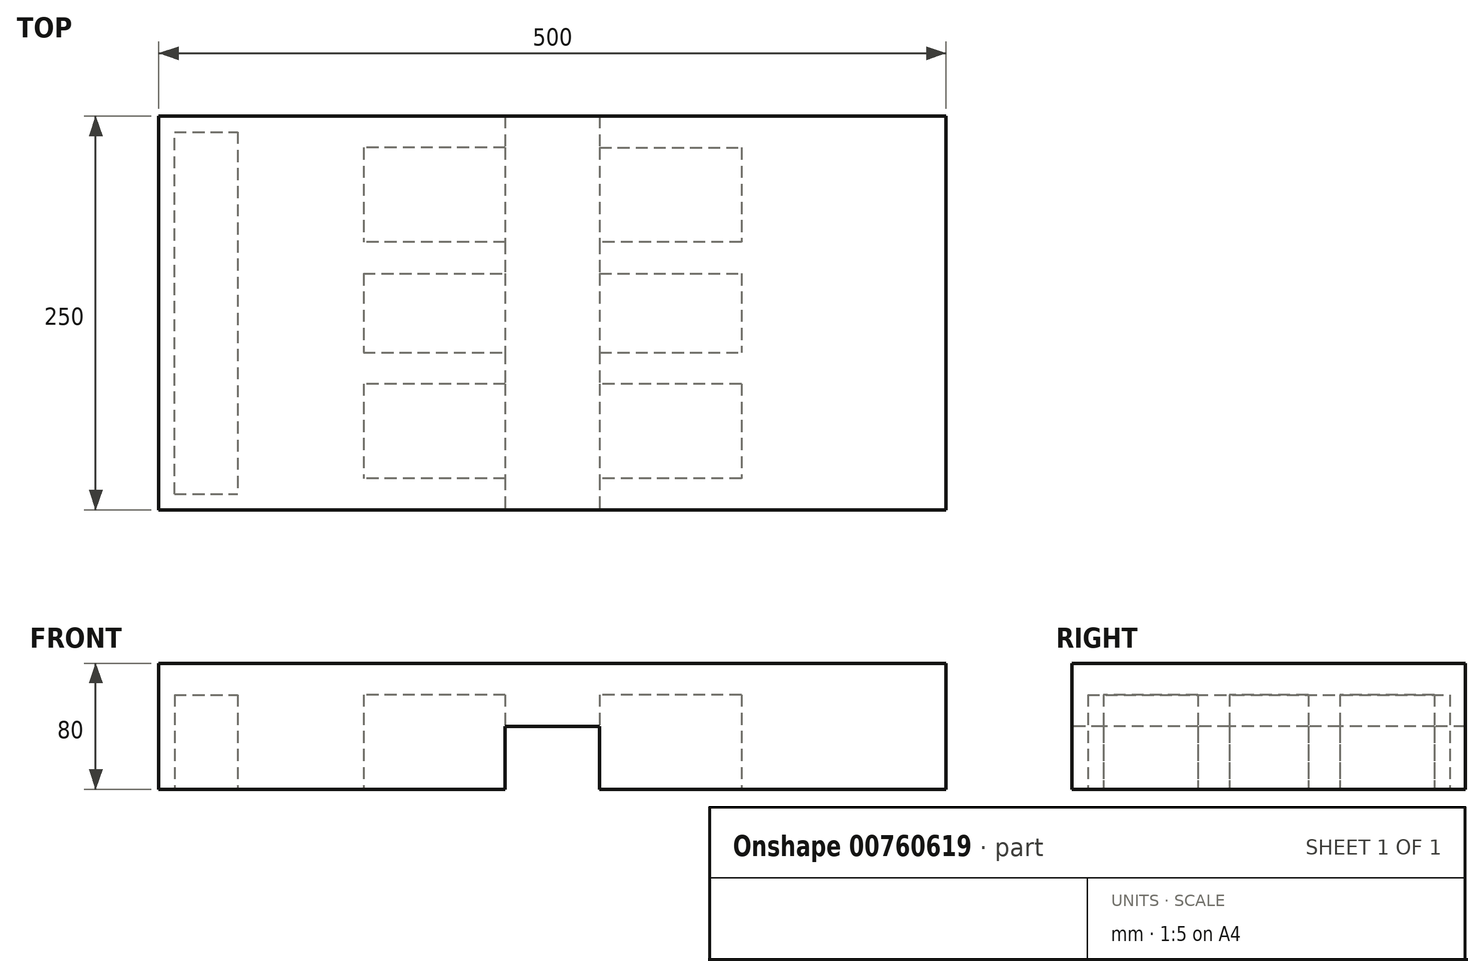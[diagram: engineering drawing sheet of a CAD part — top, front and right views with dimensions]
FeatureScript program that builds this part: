
annotation { "Feature Type Name" : "Feature", "Feature Type Description" : "" }
export const myFeature = defineFeature(function(context is Context, id is Id, definition is map)
    precondition{}
    {
        {
            var Q0;
            Q0=qCreatedBy(makeId("Top.planeOp"),FACE);
            var sketch = newSketch(context, id + "F0", { "sketchPlane" : qUnion([Q0])});
            skLineSegment(sketch, "E0.bottom", {"start": v(-250, 125) * mm, "end": v(250, 125) * mm});
            skLineSegment(sketch, "E0.top", {"start": v(-250, -125) * mm, "end": v(250, -125) * mm});
            skLineSegment(sketch, "E0.left", {"start": v(-250, 125) * mm, "end": v(-250, -125) * mm});
            skLineSegment(sketch, "E0.right", {"start": v(250, 125) * mm, "end": v(250, -125) * mm});
            skPoint(sketch, "E0.middle", {"position": v(0, 0) * mm});
            skLineSegment(sketch, "E1", {"start": v(-250, 0) * mm, "end": v(250, 0) * mm});
            skLineSegment(sketch, "E2", {"start": v(0, 125) * mm, "end": v(0, -125) * mm});
            skLineSegment(sketch, "E3", {"start": v(-30, 125) * mm, "end": v(-30, -125) * mm});
            skLineSegment(sketch, "E4", {"start": v(30, 125) * mm, "end": v(30, -125) * mm});
            skLineSegment(sketch, "E5", {"start": v(120, 125) * mm, "end": v(120, -125) * mm});
            skLineSegment(sketch, "E6", {"start": v(-120, 125) * mm, "end": v(-120, -125) * mm});
            skLineSegment(sketch, "E7", {"start": v(30, 105) * mm, "end": v(120, 105) * mm});
            skLineSegment(sketch, "E8", {"start": v(120, 45) * mm, "end": v(30, 45) * mm});
            skLineSegment(sketch, "E9", {"start": v(120, -45) * mm, "end": v(30, -45) * mm});
            skLineSegment(sketch, "E10", {"start": v(120, -105) * mm, "end": v(30, -105) * mm});
            skLineSegment(sketch, "E11", {"start": v(-30, -105) * mm, "end": v(-120, -105) * mm});
            skLineSegment(sketch, "E12", {"start": v(-30, -45) * mm, "end": v(-120, -45) * mm});
            skLineSegment(sketch, "E13", {"start": v(-30, 45) * mm, "end": v(-120, 45) * mm});
            skLineSegment(sketch, "E14", {"start": v(-30, 105) * mm, "end": v(-120, 105) * mm});
            skLineSegment(sketch, "E15", {"start": v(-120, 25) * mm, "end": v(120, 25) * mm});
            skLineSegment(sketch, "E16", {"start": v(-120, -25) * mm, "end": v(120, -25) * mm});
            skLineSegment(sketch, "E17", {"start": v(-250, 115) * mm, "end": v(-120, 115) * mm});
            skLineSegment(sketch, "E18", {"start": v(-250, -115) * mm, "end": v(-120, -115) * mm});
            skLineSegment(sketch, "E19", {"start": v(-240, -115) * mm, "end": v(-240, 115) * mm});
            skLineSegment(sketch, "E20", {"start": v(-200, 115) * mm, "end": v(-200, -115) * mm});
            skSolve(sketch);
        }
        {
            var Q0;
            {var subQ1=sQuery(id+"F0.wireOp",EDGE,"E0.bottom");var subQ5=sQuery(id+"F0.wireOp",EDGE,"E0.left");var subQ6=makeQuery(id+"F0.imprint","INTERSECT",VERTEX,{"derivedFrom":[subQ1,subQ5]});Q0=makeQuery(id+"F0.imprint","IMPRINT",FACE,{"disambiguationData":[TD([[makeQuery(id+"F0.imprint","IMPRINT",EDGE,{"disambiguationData":[TD([[subQ6,-1.0]])],"derivedFrom":subQ1}),-1.0]])]});}
            var Q1;
            {var subQ0=sQuery(id+"F0.wireOp",EDGE,"E1");var subQ1=sQuery(id+"F0.wireOp",EDGE,"E0.left");var subQ2=makeQuery(id+"F0.imprint","INTERSECT",VERTEX,{"derivedFrom":[subQ1,subQ0]});Q1=makeQuery(id+"F0.imprint","IMPRINT",FACE,{"disambiguationData":[TD([[makeQuery(id+"F0.imprint","IMPRINT",EDGE,{"disambiguationData":[TD([[subQ2,1.0]])],"derivedFrom":subQ1}),1.0]])]});}
            var Q2;
            {var subQ0=sQuery(id+"F0.wireOp",EDGE,"E1");var subQ1=sQuery(id+"F0.wireOp",EDGE,"E0.left");var subQ2=makeQuery(id+"F0.imprint","INTERSECT",VERTEX,{"derivedFrom":[subQ1,subQ0]});Q2=makeQuery(id+"F0.imprint","IMPRINT",FACE,{"disambiguationData":[TD([[makeQuery(id+"F0.imprint","IMPRINT",EDGE,{"disambiguationData":[TD([[subQ2,-1.0]])],"derivedFrom":subQ1}),1.0]])]});}
            var Q3;
            {var subQ1=sQuery(id+"F0.wireOp",EDGE,"E0.left");var subQ4=sQuery(id+"F0.wireOp",EDGE,"E0.top");var subQ5=makeQuery(id+"F0.imprint","INTERSECT",VERTEX,{"derivedFrom":[subQ4,subQ1]});Q3=makeQuery(id+"F0.imprint","IMPRINT",FACE,{"disambiguationData":[TD([[makeQuery(id+"F0.imprint","IMPRINT",EDGE,{"disambiguationData":[TD([[subQ5,-1.0]])],"derivedFrom":subQ4}),1.0]])]});}
            var Q4;
            {var subQ4=sQuery(id+"F0.wireOp",EDGE,"E14");Q4=makeQuery(id+"F0.imprint","IMPRINT",FACE,{"disambiguationData":[TD([[makeQuery(id+"F0.imprint","IMPRINT",EDGE,{"derivedFrom":subQ4}),-1.0]])]});}
            var Q5;
            {var subQ1=sQuery(id+"F0.wireOp",EDGE,"E0.bottom");var subQ5=sQuery(id+"F0.wireOp",EDGE,"E2");var subQ6=makeQuery(id+"F0.imprint","INTERSECT",VERTEX,{"derivedFrom":[subQ1,subQ5]});Q5=makeQuery(id+"F0.imprint","IMPRINT",FACE,{"disambiguationData":[TD([[makeQuery(id+"F0.imprint","IMPRINT",EDGE,{"disambiguationData":[TD([[subQ6,1.0]])],"derivedFrom":subQ1}),-1.0]])]});}
            var Q6;
            {var subQ5=sQuery(id+"F0.wireOp",EDGE,"E7");Q6=makeQuery(id+"F0.imprint","IMPRINT",FACE,{"disambiguationData":[TD([[makeQuery(id+"F0.imprint","IMPRINT",EDGE,{"derivedFrom":subQ5}),1.0]])]});}
            var Q7;
            {var subQ3=sQuery(id+"F0.wireOp",EDGE,"E2");var subQ4=sQuery(id+"F0.wireOp",EDGE,"E0.bottom");var subQ5=makeQuery(id+"F0.imprint","INTERSECT",VERTEX,{"derivedFrom":[subQ4,subQ3]});Q7=makeQuery(id+"F0.imprint","IMPRINT",FACE,{"disambiguationData":[TD([[makeQuery(id+"F0.imprint","IMPRINT",EDGE,{"disambiguationData":[TD([[subQ5,-1.0]])],"derivedFrom":subQ4}),-1.0]])]});}
            var Q8;
            {var subQ0=sQuery(id+"F0.wireOp",EDGE,"E13");Q8=makeQuery(id+"F0.imprint","IMPRINT",FACE,{"disambiguationData":[TD([[makeQuery(id+"F0.imprint","IMPRINT",EDGE,{"derivedFrom":subQ0}),1.0]])]});}
            var Q9;
            {var subQ0=sQuery(id+"F0.wireOp",EDGE,"E12");Q9=makeQuery(id+"F0.imprint","IMPRINT",FACE,{"disambiguationData":[TD([[makeQuery(id+"F0.imprint","IMPRINT",EDGE,{"derivedFrom":subQ0}),-1.0]])]});}
            var Q10;
            {var subQ4=sQuery(id+"F0.wireOp",EDGE,"E11");Q10=makeQuery(id+"F0.imprint","IMPRINT",FACE,{"disambiguationData":[TD([[makeQuery(id+"F0.imprint","IMPRINT",EDGE,{"derivedFrom":subQ4}),1.0]])]});}
            var Q11;
            {var subQ5=sQuery(id+"F0.wireOp",EDGE,"E2");var subQ6=sQuery(id+"F0.wireOp",EDGE,"E0.top");var subQ7=makeQuery(id+"F0.imprint","INTERSECT",VERTEX,{"derivedFrom":[subQ6,subQ5]});Q11=makeQuery(id+"F0.imprint","IMPRINT",FACE,{"disambiguationData":[TD([[makeQuery(id+"F0.imprint","IMPRINT",EDGE,{"disambiguationData":[TD([[subQ7,1.0]])],"derivedFrom":subQ6}),1.0]])]});}
            var Q12;
            {var subQ5=sQuery(id+"F0.wireOp",EDGE,"E2");var subQ6=sQuery(id+"F0.wireOp",EDGE,"E0.top");var subQ7=makeQuery(id+"F0.imprint","INTERSECT",VERTEX,{"derivedFrom":[subQ6,subQ5]});Q12=makeQuery(id+"F0.imprint","IMPRINT",FACE,{"disambiguationData":[TD([[makeQuery(id+"F0.imprint","IMPRINT",EDGE,{"disambiguationData":[TD([[subQ7,-1.0]])],"derivedFrom":subQ6}),1.0]])]});}
            var Q13;
            {var subQ0=sQuery(id+"F0.wireOp",EDGE,"E9");Q13=makeQuery(id+"F0.imprint","IMPRINT",FACE,{"disambiguationData":[TD([[makeQuery(id+"F0.imprint","IMPRINT",EDGE,{"derivedFrom":subQ0}),-1.0]])]});}
            var Q14;
            {var subQ0=sQuery(id+"F0.wireOp",EDGE,"E8");Q14=makeQuery(id+"F0.imprint","IMPRINT",FACE,{"disambiguationData":[TD([[makeQuery(id+"F0.imprint","IMPRINT",EDGE,{"derivedFrom":subQ0}),1.0]])]});}
            var Q15;
            {var subQ5=sQuery(id+"F0.wireOp",EDGE,"E10");Q15=makeQuery(id+"F0.imprint","IMPRINT",FACE,{"disambiguationData":[TD([[makeQuery(id+"F0.imprint","IMPRINT",EDGE,{"derivedFrom":subQ5}),1.0]])]});}
            var Q16;
            {var subQ1=sQuery(id+"F0.wireOp",EDGE,"E0.bottom");var subQ4=sQuery(id+"F0.wireOp",EDGE,"E0.right");var subQ5=makeQuery(id+"F0.imprint","INTERSECT",VERTEX,{"derivedFrom":[subQ1,subQ4]});Q16=makeQuery(id+"F0.imprint","IMPRINT",FACE,{"disambiguationData":[TD([[makeQuery(id+"F0.imprint","IMPRINT",EDGE,{"disambiguationData":[TD([[subQ5,1.0]])],"derivedFrom":subQ1}),-1.0]])]});}
            var Q17;
            {var subQ4=sQuery(id+"F0.wireOp",EDGE,"E0.right");var subQ5=sQuery(id+"F0.wireOp",EDGE,"E0.top");var subQ6=makeQuery(id+"F0.imprint","INTERSECT",VERTEX,{"derivedFrom":[subQ5,subQ4]});Q17=makeQuery(id+"F0.imprint","IMPRINT",FACE,{"disambiguationData":[TD([[makeQuery(id+"F0.imprint","IMPRINT",EDGE,{"disambiguationData":[TD([[subQ6,1.0]])],"derivedFrom":subQ5}),1.0]])]});}
            var Q18;
            {var subQ6=sQuery(id+"F0.wireOp",EDGE,"E20");var subQ8=sQuery(id+"F0.wireOp",EDGE,"E1");var subQ9=makeQuery(id+"F0.imprint","INTERSECT",VERTEX,{"derivedFrom":[subQ8,subQ6]});Q18=makeQuery(id+"F0.imprint","IMPRINT",FACE,{"disambiguationData":[TD([[makeQuery(id+"F0.imprint","IMPRINT",EDGE,{"disambiguationData":[TD([[subQ9,-1.0]])],"derivedFrom":subQ8}),1.0]])]});}
            var Q19;
            {var subQ4=sQuery(id+"F0.wireOp",EDGE,"E1");var subQ6=sQuery(id+"F0.wireOp",EDGE,"E20");var subQ7=makeQuery(id+"F0.imprint","INTERSECT",VERTEX,{"derivedFrom":[subQ4,subQ6]});Q19=makeQuery(id+"F0.imprint","IMPRINT",FACE,{"disambiguationData":[TD([[makeQuery(id+"F0.imprint","IMPRINT",EDGE,{"disambiguationData":[TD([[subQ7,-1.0]])],"derivedFrom":subQ4}),-1.0]])]});}
            var Q20;
            {var subQ0=sQuery(id+"F0.wireOp",EDGE,"E19");var subQ1=sQuery(id+"F0.wireOp",EDGE,"E1");var subQ2=makeQuery(id+"F0.imprint","INTERSECT",VERTEX,{"derivedFrom":[subQ1,subQ0]});Q20=makeQuery(id+"F0.imprint","IMPRINT",FACE,{"disambiguationData":[TD([[makeQuery(id+"F0.imprint","IMPRINT",EDGE,{"disambiguationData":[TD([[subQ2,-1.0]])],"derivedFrom":subQ1}),1.0]])]});}
            var Q21;
            {var subQ0=sQuery(id+"F0.wireOp",EDGE,"E19");var subQ1=sQuery(id+"F0.wireOp",EDGE,"E1");var subQ2=makeQuery(id+"F0.imprint","INTERSECT",VERTEX,{"derivedFrom":[subQ1,subQ0]});Q21=makeQuery(id+"F0.imprint","IMPRINT",FACE,{"disambiguationData":[TD([[makeQuery(id+"F0.imprint","IMPRINT",EDGE,{"disambiguationData":[TD([[subQ2,-1.0]])],"derivedFrom":subQ1}),-1.0]])]});}
            var Q22;
            {var subQ0=sQuery(id+"F0.wireOp",EDGE,"E13");Q22=makeQuery(id+"F0.imprint","IMPRINT",FACE,{"disambiguationData":[TD([[makeQuery(id+"F0.imprint","IMPRINT",EDGE,{"derivedFrom":subQ0}),-1.0]])]});}
            var Q23;
            {var subQ0=sQuery(id+"F0.wireOp",EDGE,"E6");var subQ1=sQuery(id+"F0.wireOp",EDGE,"E1");var subQ2=makeQuery(id+"F0.imprint","INTERSECT",VERTEX,{"derivedFrom":[subQ1,subQ0]});Q23=makeQuery(id+"F0.imprint","IMPRINT",FACE,{"disambiguationData":[TD([[makeQuery(id+"F0.imprint","IMPRINT",EDGE,{"disambiguationData":[TD([[subQ2,-1.0]])],"derivedFrom":subQ1}),1.0]])]});}
            var Q24;
            {var subQ0=sQuery(id+"F0.wireOp",EDGE,"E6");var subQ1=sQuery(id+"F0.wireOp",EDGE,"E1");var subQ2=makeQuery(id+"F0.imprint","INTERSECT",VERTEX,{"derivedFrom":[subQ1,subQ0]});Q24=makeQuery(id+"F0.imprint","IMPRINT",FACE,{"disambiguationData":[TD([[makeQuery(id+"F0.imprint","IMPRINT",EDGE,{"disambiguationData":[TD([[subQ2,-1.0]])],"derivedFrom":subQ1}),-1.0]])]});}
            var Q25;
            {var subQ0=sQuery(id+"F0.wireOp",EDGE,"E11");Q25=makeQuery(id+"F0.imprint","IMPRINT",FACE,{"disambiguationData":[TD([[makeQuery(id+"F0.imprint","IMPRINT",EDGE,{"derivedFrom":subQ0}),-1.0]])]});}
            var Q26;
            {var subQ0=sQuery(id+"F0.wireOp",EDGE,"E3");var subQ1=sQuery(id+"F0.wireOp",EDGE,"E1");var subQ2=makeQuery(id+"F0.imprint","INTERSECT",VERTEX,{"derivedFrom":[subQ1,subQ0]});Q26=makeQuery(id+"F0.imprint","IMPRINT",FACE,{"disambiguationData":[TD([[makeQuery(id+"F0.imprint","IMPRINT",EDGE,{"disambiguationData":[TD([[subQ2,-1.0]])],"derivedFrom":subQ1}),-1.0]])]});}
            var Q27;
            {var subQ0=sQuery(id+"F0.wireOp",EDGE,"E3");var subQ1=sQuery(id+"F0.wireOp",EDGE,"E1");var subQ2=makeQuery(id+"F0.imprint","INTERSECT",VERTEX,{"derivedFrom":[subQ1,subQ0]});Q27=makeQuery(id+"F0.imprint","IMPRINT",FACE,{"disambiguationData":[TD([[makeQuery(id+"F0.imprint","IMPRINT",EDGE,{"disambiguationData":[TD([[subQ2,-1.0]])],"derivedFrom":subQ1}),1.0]])]});}
            var Q28;
            {var subQ0=sQuery(id+"F0.wireOp",EDGE,"E2");var subQ1=sQuery(id+"F0.wireOp",EDGE,"E1");var subQ2=makeQuery(id+"F0.imprint","INTERSECT",VERTEX,{"derivedFrom":[subQ1,subQ0]});Q28=makeQuery(id+"F0.imprint","IMPRINT",FACE,{"disambiguationData":[TD([[makeQuery(id+"F0.imprint","IMPRINT",EDGE,{"disambiguationData":[TD([[subQ2,-1.0]])],"derivedFrom":subQ1}),1.0]])]});}
            var Q29;
            {var subQ0=sQuery(id+"F0.wireOp",EDGE,"E4");var subQ1=sQuery(id+"F0.wireOp",EDGE,"E1");var subQ2=makeQuery(id+"F0.imprint","INTERSECT",VERTEX,{"derivedFrom":[subQ1,subQ0]});Q29=makeQuery(id+"F0.imprint","IMPRINT",FACE,{"disambiguationData":[TD([[makeQuery(id+"F0.imprint","IMPRINT",EDGE,{"disambiguationData":[TD([[subQ2,-1.0]])],"derivedFrom":subQ1}),1.0]])]});}
            var Q30;
            {var subQ0=sQuery(id+"F0.wireOp",EDGE,"E9");Q30=makeQuery(id+"F0.imprint","IMPRINT",FACE,{"disambiguationData":[TD([[makeQuery(id+"F0.imprint","IMPRINT",EDGE,{"derivedFrom":subQ0}),1.0]])]});}
            var Q31;
            {var subQ0=sQuery(id+"F0.wireOp",EDGE,"E4");var subQ1=sQuery(id+"F0.wireOp",EDGE,"E1");var subQ2=makeQuery(id+"F0.imprint","INTERSECT",VERTEX,{"derivedFrom":[subQ1,subQ0]});Q31=makeQuery(id+"F0.imprint","IMPRINT",FACE,{"disambiguationData":[TD([[makeQuery(id+"F0.imprint","IMPRINT",EDGE,{"disambiguationData":[TD([[subQ2,-1.0]])],"derivedFrom":subQ1}),-1.0]])]});}
            var Q32;
            {var subQ0=sQuery(id+"F0.wireOp",EDGE,"E2");var subQ1=sQuery(id+"F0.wireOp",EDGE,"E1");var subQ2=makeQuery(id+"F0.imprint","INTERSECT",VERTEX,{"derivedFrom":[subQ1,subQ0]});Q32=makeQuery(id+"F0.imprint","IMPRINT",FACE,{"disambiguationData":[TD([[makeQuery(id+"F0.imprint","IMPRINT",EDGE,{"disambiguationData":[TD([[subQ2,-1.0]])],"derivedFrom":subQ1}),-1.0]])]});}
            var Q33;
            {var subQ0=sQuery(id+"F0.wireOp",EDGE,"E7");Q33=makeQuery(id+"F0.imprint","IMPRINT",FACE,{"disambiguationData":[TD([[makeQuery(id+"F0.imprint","IMPRINT",EDGE,{"derivedFrom":subQ0}),-1.0]])]});}
            extrude(context, id + "F1", {"entities" : qUnion([Q0, Q1, Q2, Q3, Q4, Q5, Q6, Q7, Q8, Q9, Q10, Q11, Q12, Q13, Q14, Q15, Q16, Q17, Q18, Q19, Q20, Q21, Q22, Q23, Q24, Q25, Q26, Q27, Q28, Q29, Q30, Q31, Q32, Q33]), "depth" : 80 * mm, "offsetDistance" : 25 * mm});
        }
        {
            var Q0;
            {var subQ0=sQuery(id+"F0.wireOp",EDGE,"E19");var subQ1=sQuery(id+"F0.wireOp",EDGE,"E1");var subQ2=makeQuery(id+"F0.imprint","INTERSECT",VERTEX,{"derivedFrom":[subQ1,subQ0]});Q0=makeQuery(id+"F0.imprint","IMPRINT",FACE,{"disambiguationData":[TD([[makeQuery(id+"F0.imprint","IMPRINT",EDGE,{"disambiguationData":[TD([[subQ2,-1.0]])],"derivedFrom":subQ1}),-1.0]])]});}
            var Q1;
            {var subQ0=sQuery(id+"F0.wireOp",EDGE,"E19");var subQ1=sQuery(id+"F0.wireOp",EDGE,"E1");var subQ2=makeQuery(id+"F0.imprint","INTERSECT",VERTEX,{"derivedFrom":[subQ1,subQ0]});Q1=makeQuery(id+"F0.imprint","IMPRINT",FACE,{"disambiguationData":[TD([[makeQuery(id+"F0.imprint","IMPRINT",EDGE,{"disambiguationData":[TD([[subQ2,-1.0]])],"derivedFrom":subQ1}),1.0]])]});}
            var Q2;
            {var subQ0=sQuery(id+"F0.wireOp",EDGE,"E9");Q2=makeQuery(id+"F0.imprint","IMPRINT",FACE,{"disambiguationData":[TD([[makeQuery(id+"F0.imprint","IMPRINT",EDGE,{"derivedFrom":subQ0}),1.0]])]});}
            var Q3;
            {var subQ0=sQuery(id+"F0.wireOp",EDGE,"E11");Q3=makeQuery(id+"F0.imprint","IMPRINT",FACE,{"disambiguationData":[TD([[makeQuery(id+"F0.imprint","IMPRINT",EDGE,{"derivedFrom":subQ0}),-1.0]])]});}
            var Q4;
            {var subQ0=sQuery(id+"F0.wireOp",EDGE,"E7");Q4=makeQuery(id+"F0.imprint","IMPRINT",FACE,{"disambiguationData":[TD([[makeQuery(id+"F0.imprint","IMPRINT",EDGE,{"derivedFrom":subQ0}),-1.0]])]});}
            var Q5;
            {var subQ0=sQuery(id+"F0.wireOp",EDGE,"E13");Q5=makeQuery(id+"F0.imprint","IMPRINT",FACE,{"disambiguationData":[TD([[makeQuery(id+"F0.imprint","IMPRINT",EDGE,{"derivedFrom":subQ0}),-1.0]])]});}
            var Q6;
            {var subQ0=sQuery(id+"F0.wireOp",EDGE,"E6");var subQ1=sQuery(id+"F0.wireOp",EDGE,"E1");var subQ2=makeQuery(id+"F0.imprint","INTERSECT",VERTEX,{"derivedFrom":[subQ1,subQ0]});Q6=makeQuery(id+"F0.imprint","IMPRINT",FACE,{"disambiguationData":[TD([[makeQuery(id+"F0.imprint","IMPRINT",EDGE,{"disambiguationData":[TD([[subQ2,-1.0]])],"derivedFrom":subQ1}),-1.0]])]});}
            var Q7;
            {var subQ0=sQuery(id+"F0.wireOp",EDGE,"E6");var subQ1=sQuery(id+"F0.wireOp",EDGE,"E1");var subQ2=makeQuery(id+"F0.imprint","INTERSECT",VERTEX,{"derivedFrom":[subQ1,subQ0]});Q7=makeQuery(id+"F0.imprint","IMPRINT",FACE,{"disambiguationData":[TD([[makeQuery(id+"F0.imprint","IMPRINT",EDGE,{"disambiguationData":[TD([[subQ2,-1.0]])],"derivedFrom":subQ1}),1.0]])]});}
            var Q8;
            {var subQ0=sQuery(id+"F0.wireOp",EDGE,"E4");var subQ1=sQuery(id+"F0.wireOp",EDGE,"E1");var subQ2=makeQuery(id+"F0.imprint","INTERSECT",VERTEX,{"derivedFrom":[subQ1,subQ0]});Q8=makeQuery(id+"F0.imprint","IMPRINT",FACE,{"disambiguationData":[TD([[makeQuery(id+"F0.imprint","IMPRINT",EDGE,{"disambiguationData":[TD([[subQ2,-1.0]])],"derivedFrom":subQ1}),-1.0]])]});}
            var Q9;
            {var subQ0=sQuery(id+"F0.wireOp",EDGE,"E4");var subQ1=sQuery(id+"F0.wireOp",EDGE,"E1");var subQ2=makeQuery(id+"F0.imprint","INTERSECT",VERTEX,{"derivedFrom":[subQ1,subQ0]});Q9=makeQuery(id+"F0.imprint","IMPRINT",FACE,{"disambiguationData":[TD([[makeQuery(id+"F0.imprint","IMPRINT",EDGE,{"disambiguationData":[TD([[subQ2,-1.0]])],"derivedFrom":subQ1}),1.0]])]});}
            extrude(context, id + "F2", {"entities" : qUnion([Q0, Q1, Q2, Q3, Q4, Q5, Q6, Q7, Q8, Q9]), "operationType" : NewBodyOperationType.REMOVE, "depth" : 60 * mm, "offsetDistance" : 25 * mm});
        }
        {
            var Q0;
            {var subQ5=sQuery(id+"F0.wireOp",EDGE,"E2");var subQ6=sQuery(id+"F0.wireOp",EDGE,"E0.top");var subQ7=makeQuery(id+"F0.imprint","INTERSECT",VERTEX,{"derivedFrom":[subQ6,subQ5]});Q0=makeQuery(id+"F0.imprint","IMPRINT",FACE,{"disambiguationData":[TD([[makeQuery(id+"F0.imprint","IMPRINT",EDGE,{"disambiguationData":[TD([[subQ7,1.0]])],"derivedFrom":subQ6}),1.0]])]});}
            var Q1;
            {var subQ3=sQuery(id+"F0.wireOp",EDGE,"E2");var subQ4=sQuery(id+"F0.wireOp",EDGE,"E0.bottom");var subQ5=makeQuery(id+"F0.imprint","INTERSECT",VERTEX,{"derivedFrom":[subQ4,subQ3]});Q1=makeQuery(id+"F0.imprint","IMPRINT",FACE,{"disambiguationData":[TD([[makeQuery(id+"F0.imprint","IMPRINT",EDGE,{"disambiguationData":[TD([[subQ5,-1.0]])],"derivedFrom":subQ4}),-1.0]])]});}
            var Q2;
            {var subQ1=sQuery(id+"F0.wireOp",EDGE,"E0.bottom");var subQ5=sQuery(id+"F0.wireOp",EDGE,"E2");var subQ6=makeQuery(id+"F0.imprint","INTERSECT",VERTEX,{"derivedFrom":[subQ1,subQ5]});Q2=makeQuery(id+"F0.imprint","IMPRINT",FACE,{"disambiguationData":[TD([[makeQuery(id+"F0.imprint","IMPRINT",EDGE,{"disambiguationData":[TD([[subQ6,1.0]])],"derivedFrom":subQ1}),-1.0]])]});}
            var Q3;
            {var subQ0=sQuery(id+"F0.wireOp",EDGE,"E3");var subQ1=sQuery(id+"F0.wireOp",EDGE,"E1");var subQ2=makeQuery(id+"F0.imprint","INTERSECT",VERTEX,{"derivedFrom":[subQ1,subQ0]});Q3=makeQuery(id+"F0.imprint","IMPRINT",FACE,{"disambiguationData":[TD([[makeQuery(id+"F0.imprint","IMPRINT",EDGE,{"disambiguationData":[TD([[subQ2,-1.0]])],"derivedFrom":subQ1}),1.0]])]});}
            var Q4;
            {var subQ0=sQuery(id+"F0.wireOp",EDGE,"E3");var subQ1=sQuery(id+"F0.wireOp",EDGE,"E1");var subQ2=makeQuery(id+"F0.imprint","INTERSECT",VERTEX,{"derivedFrom":[subQ1,subQ0]});Q4=makeQuery(id+"F0.imprint","IMPRINT",FACE,{"disambiguationData":[TD([[makeQuery(id+"F0.imprint","IMPRINT",EDGE,{"disambiguationData":[TD([[subQ2,-1.0]])],"derivedFrom":subQ1}),-1.0]])]});}
            var Q5;
            {var subQ0=sQuery(id+"F0.wireOp",EDGE,"E2");var subQ1=sQuery(id+"F0.wireOp",EDGE,"E1");var subQ2=makeQuery(id+"F0.imprint","INTERSECT",VERTEX,{"derivedFrom":[subQ1,subQ0]});Q5=makeQuery(id+"F0.imprint","IMPRINT",FACE,{"disambiguationData":[TD([[makeQuery(id+"F0.imprint","IMPRINT",EDGE,{"disambiguationData":[TD([[subQ2,-1.0]])],"derivedFrom":subQ1}),-1.0]])]});}
            var Q6;
            {var subQ0=sQuery(id+"F0.wireOp",EDGE,"E2");var subQ1=sQuery(id+"F0.wireOp",EDGE,"E1");var subQ2=makeQuery(id+"F0.imprint","INTERSECT",VERTEX,{"derivedFrom":[subQ1,subQ0]});Q6=makeQuery(id+"F0.imprint","IMPRINT",FACE,{"disambiguationData":[TD([[makeQuery(id+"F0.imprint","IMPRINT",EDGE,{"disambiguationData":[TD([[subQ2,-1.0]])],"derivedFrom":subQ1}),1.0]])]});}
            var Q7;
            {var subQ5=sQuery(id+"F0.wireOp",EDGE,"E2");var subQ6=sQuery(id+"F0.wireOp",EDGE,"E0.top");var subQ7=makeQuery(id+"F0.imprint","INTERSECT",VERTEX,{"derivedFrom":[subQ6,subQ5]});Q7=makeQuery(id+"F0.imprint","IMPRINT",FACE,{"disambiguationData":[TD([[makeQuery(id+"F0.imprint","IMPRINT",EDGE,{"disambiguationData":[TD([[subQ7,-1.0]])],"derivedFrom":subQ6}),1.0]])]});}
            extrude(context, id + "F3", {"entities" : qUnion([Q0, Q1, Q2, Q3, Q4, Q5, Q6, Q7]), "operationType" : NewBodyOperationType.REMOVE, "depth" : 40 * mm, "offsetDistance" : 25 * mm});
        }
    });
